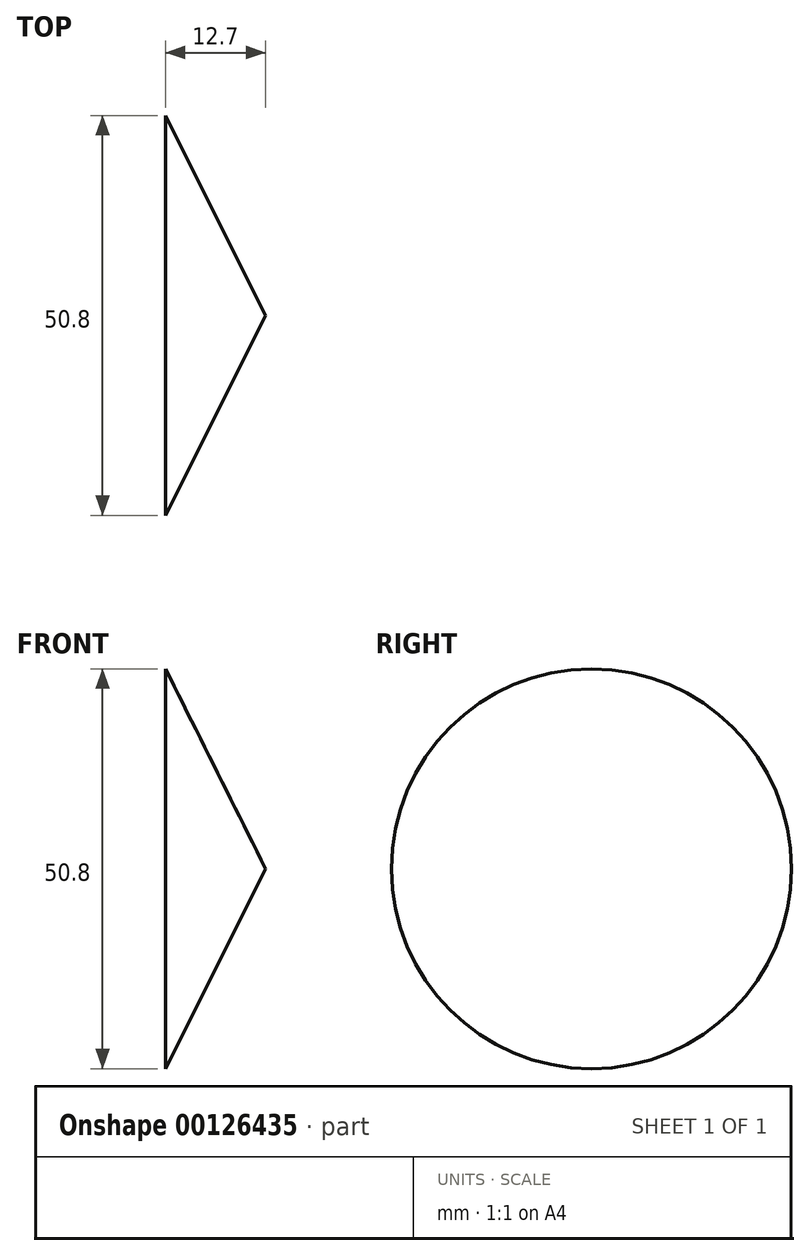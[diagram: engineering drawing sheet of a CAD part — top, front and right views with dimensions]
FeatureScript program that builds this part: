
annotation { "Feature Type Name" : "Feature", "Feature Type Description" : "" }
export const myFeature = defineFeature(function(context is Context, id is Id, definition is map)
    precondition{}
    {
        {
            var Q0;
            Q0=qCreatedBy(makeId("Top.planeOp"),FACE);
            var sketch = newSketch(context, id + "F0", { "sketchPlane" : qUnion([Q0])});
            skLineSegment(sketch, "E0", {"start": v(0, 0) * mm, "end": v(12.7, 0) * mm});
            skLineSegment(sketch, "E1", {"start": v(0, 0) * mm, "end": v(0, 25.4) * mm});
            skLineSegment(sketch, "E2", {"start": v(0, 25.4) * mm, "end": v(12.7, 0) * mm});
            skSolve(sketch);
        }
        {
            var Q0;
            Q0 = qSketchRegion(id + "F0", true);
            var Q1;
            Q1=sQuery(id+"F0.wireOp",EDGE,"E0");
            revolve(context, id + "F1", {"entities" : qUnion([Q0]), "axis" : qUnion([Q1]), "revolveType" : RevolveType.FULL});
        }
    });
